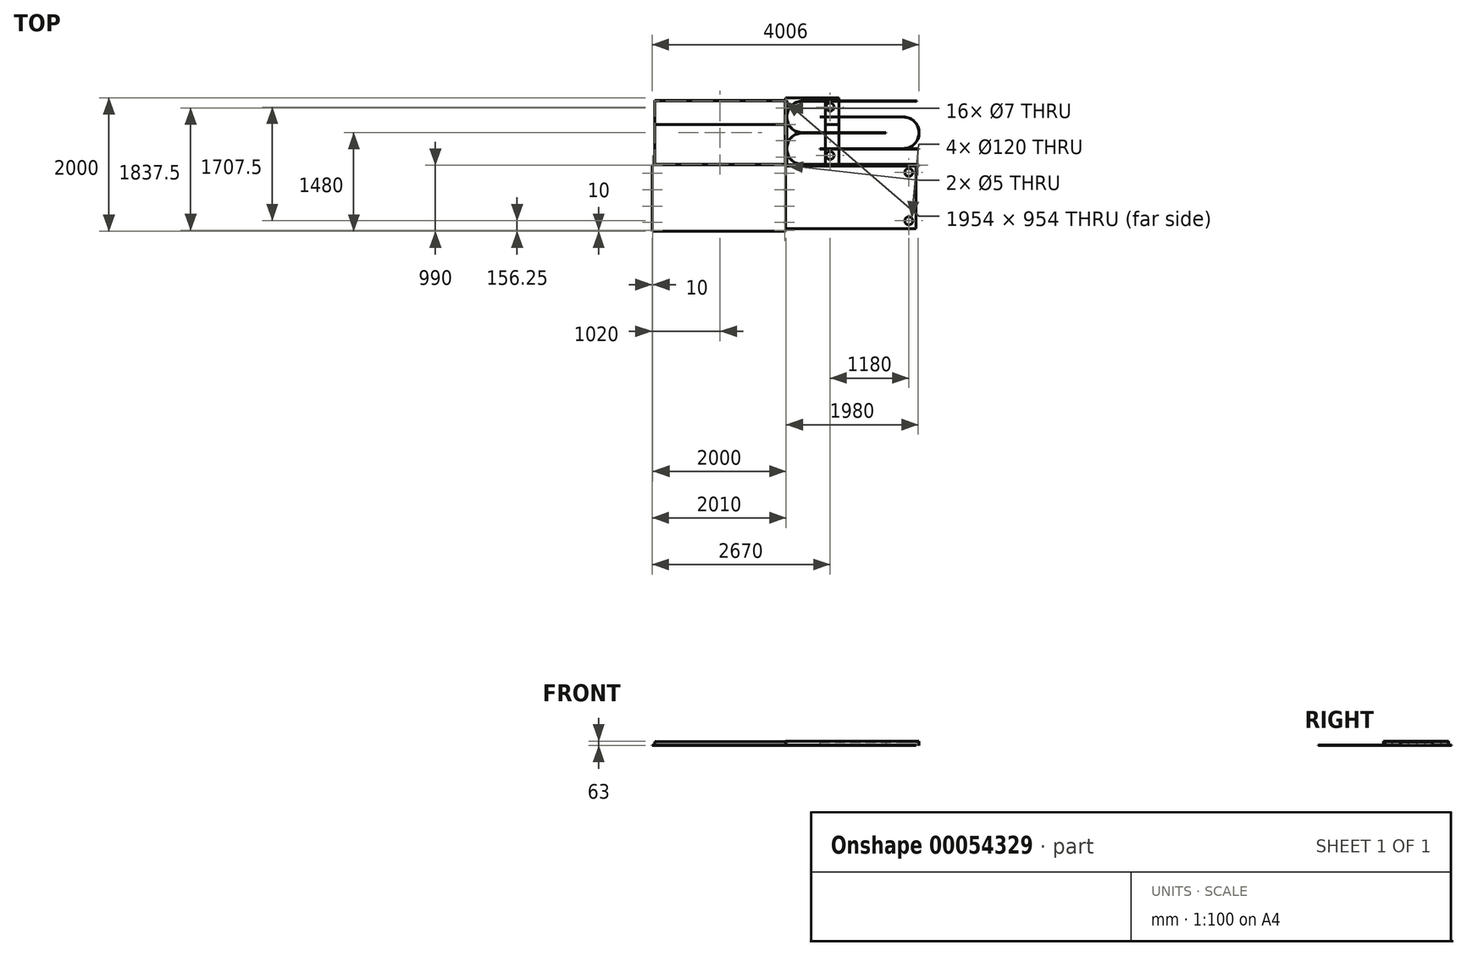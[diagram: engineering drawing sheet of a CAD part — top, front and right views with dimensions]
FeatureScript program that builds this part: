
annotation { "Feature Type Name" : "Feature", "Feature Type Description" : "" }
export const myFeature = defineFeature(function(context is Context, id is Id, definition is map)
    precondition{}
    {
        {
            var Q0;
            Q0=qCreatedBy(makeId("Top.planeOp"),FACE);
            var sketch = newSketch(context, id + "F0", { "sketchPlane" : qUnion([Q0])});
            skLineSegment(sketch, "E0.bottom", {"start": v(0, 0) * mm, "end": v(600, 0) * mm});
            skLineSegment(sketch, "E0.top", {"start": v(0, 1000) * mm, "end": v(600, 1000) * mm});
            skLineSegment(sketch, "E0.left", {"start": v(0, 0) * mm, "end": v(0, 1000) * mm});
            skLineSegment(sketch, "E0.right", {"start": v(600, 0) * mm, "end": v(600, 1000) * mm});
            skSolve(sketch);
        }
        {
            var Q0;
            Q0=makeQuery(id+"F0.imprint","IMPRINT",FACE,{"disambiguationData":[TD([[makeQuery(id+"F0.imprint","IMPRINT",EDGE,{"derivedFrom":sQuery(id+"F0.wireOp",EDGE,"E0.bottom")}),1.0]])]});
            extrude(context, id + "F1", {"entities" : qUnion([Q0]), "depth" : 3 * mm});
        }
        {
            var Q0;
            Q0=qCreatedBy(makeId("Top.planeOp"),FACE);
            var sketch = newSketch(context, id + "F2", { "sketchPlane" : qUnion([Q0])});
            skLineSegment(sketch, "E1.bottom", {"start": v(600, 0) * mm, "end": v(800, 0) * mm});
            skLineSegment(sketch, "E1.top", {"start": v(600, 600) * mm, "end": v(800, 600) * mm});
            skLineSegment(sketch, "E1.left", {"start": v(600, 0) * mm, "end": v(600, 600) * mm});
            skLineSegment(sketch, "E1.right", {"start": v(800, 0) * mm, "end": v(800, 600) * mm});
            skCircle(sketch, "E2", {"center": v(670, 136.25) * mm, "radius": 60 * mm});
            skSolve(sketch);
        }
        {
            var Q0;
            Q0=makeQuery(id+"F2.imprint","IMPRINT",FACE,{"disambiguationData":[TD([[makeQuery(id+"F2.imprint","IMPRINT",EDGE,{"derivedFrom":sQuery(id+"F2.wireOp",EDGE,"E1.bottom")}),1.0]])]});
            extrude(context, id + "F3", {"entities" : qUnion([Q0]), "depth" : 3 * mm});
        }
        {
            var Q0;
            Q0=qCreatedBy(makeId("Top.planeOp"),FACE);
            var sketch = newSketch(context, id + "F4", { "sketchPlane" : qUnion([Q0])});
            skLineSegment(sketch, "E3.bottom", {"start": v(600, 1000) * mm, "end": v(800, 1000) * mm});
            skLineSegment(sketch, "E3.top", {"start": v(600, 600) * mm, "end": v(800, 600) * mm});
            skLineSegment(sketch, "E3.left", {"start": v(600, 1000) * mm, "end": v(600, 600) * mm});
            skLineSegment(sketch, "E3.right", {"start": v(800, 1000) * mm, "end": v(800, 600) * mm});
            skCircle(sketch, "E4", {"center": v(670, 863.75) * mm, "radius": 60 * mm});
            skSolve(sketch);
        }
        {
            var Q0;
            Q0=makeQuery(id+"F4.imprint","IMPRINT",FACE,{"disambiguationData":[TD([[makeQuery(id+"F4.imprint","IMPRINT",EDGE,{"derivedFrom":sQuery(id+"F4.wireOp",EDGE,"E3.bottom")}),-1.0]])]});
            extrude(context, id + "F5", {"entities" : qUnion([Q0]), "depth" : 3 * mm});
        }
        {
            var Q0;
            Q0=makeQuery(id+"F1.opExtrude","CAP_FACE",FACE,{"disambiguationData":[OSD([sQuery(id+"F0.wireOp",EDGE,"E0.bottom"),sQuery(id+"F0.wireOp",EDGE,"E0.top"),sQuery(id+"F0.wireOp",EDGE,"E0.left"),sQuery(id+"F0.wireOp",EDGE,"E0.right")])],"isStart":false});
            var sketch = newSketch(context, id + "F6", { "sketchPlane" : qUnion([Q0])});
            skArc(sketch, "E5", {"start": v(257, 477) * mm, "mid": v(18.5, 238.5) * mm, "end": v(257, 0) * mm});
            skLineSegment(sketch, "E6", {"start": v(257, 0) * mm, "end": v(1972.5, 0) * mm});
            skLineSegment(sketch, "E7", {"start": v(257, 238.5) * mm, "end": v(1240.98, 238.5) * mm, "construction": true});
            skLineSegment(sketch, "E8", {"start": v(257, 477) * mm, "end": v(1510.5, 477) * mm});
            skLineSegment(sketch, "E9.0", {"start": v(257, 474) * mm, "end": v(1510.5, 474) * mm});
            skArc(sketch, "E9.1", {"start": v(257, 474) * mm, "mid": v(21.5, 238.5) * mm, "end": v(257, 3) * mm});
            skLineSegment(sketch, "E9.2", {"start": v(257, 3) * mm, "end": v(1972.5, 3) * mm});
            skLineSegment(sketch, "E10", {"start": v(1510.5, 477) * mm, "end": v(1510.5, 474) * mm});
            skLineSegment(sketch, "E11", {"start": v(1972.5, 3) * mm, "end": v(1972.5, 0) * mm});
            skLineSegment(sketch, "E12.0", {"start": v(257, 475.5) * mm, "end": v(1510.5, 475.5) * mm, "construction": true});
            skArc(sketch, "E12.1", {"start": v(257, 475.5) * mm, "mid": v(20, 238.5) * mm, "end": v(257, 1.5) * mm, "construction": true});
            skLineSegment(sketch, "E12.2", {"start": v(257, 1.5) * mm, "end": v(1972.5, 1.5) * mm, "construction": true});
            skSolve(sketch);
        }
        {
            var Q0;
            {var subQ0=sQuery(id+"F6.wireOp",EDGE,"E10");Q0=makeQuery(id+"F6.imprint","IMPRINT",FACE,{"disambiguationData":[TD([[makeQuery(id+"F6.imprint","IMPRINT",EDGE,{"derivedFrom":subQ0}),-1.0]])]});}
            var Q1;
            {var subQ10=sQuery(id+"F6.wireOp",EDGE,"E9.1");Q1=makeQuery(id+"F6.imprint","IMPRINT",FACE,{"disambiguationData":[TD([[makeQuery(id+"F6.imprint","IMPRINT",EDGE,{"derivedFrom":subQ10}),-1.0]])]});}
            var Q2;
            {var subQ3=sQuery(id+"F6.wireOp",EDGE,"E11");Q2=makeQuery(id+"F6.imprint","IMPRINT",FACE,{"disambiguationData":[TD([[makeQuery(id+"F6.imprint","IMPRINT",EDGE,{"derivedFrom":subQ3}),-1.0]])]});}
            extrude(context, id + "F7", {"entities" : qUnion([Q0, Q1, Q2]), "depth" : 50 * mm});
        }
        {
            var Q0;
            Q0=makeQuery(id+"F7.opExtrude","SWEPT_BODY",BODY,{"disambiguationData":[OSD([sQuery(id+"F6.wireOp",EDGE,"E5"),sQuery(id+"F6.wireOp",EDGE,"E6"),sQuery(id+"F6.wireOp",EDGE,"E8"),sQuery(id+"F6.wireOp",EDGE,"E9.0"),sQuery(id+"F6.wireOp",EDGE,"E9.1"),sQuery(id+"F6.wireOp",EDGE,"E9.2"),sQuery(id+"F6.wireOp",EDGE,"E10"),sQuery(id+"F6.wireOp",EDGE,"E11")])]});
            var Q1;
            Q1=makeQuery(id+"F7.opExtrude","SWEPT_FACE",FACE,{"disambiguationData":[OSD([sQuery(id+"F6.wireOp",EDGE,"E8")])]});
            mirror(context, id + "F8", {"entities" : qUnion([Q0]), "mirrorPlane" : qUnion([Q1])});
        }
        {
            var Q0;
            Q0=qCreatedBy(makeId("Top.planeOp"),FACE);
            var sketch = newSketch(context, id + "F9", { "sketchPlane" : qUnion([Q0])});
            skArc(sketch, "E13", {"start": v(1767.5, 238.5) * mm, "mid": v(2006, 477) * mm, "end": v(1767.5, 715.5) * mm});
            skLineSegment(sketch, "E14", {"start": v(1767.5, 715.5) * mm, "end": v(514, 715.5) * mm});
            skLineSegment(sketch, "E15", {"start": v(1906.7, 477) * mm, "end": v(1767.5, 477) * mm, "construction": true});
            skLineSegment(sketch, "E16.MirrorCS", {"start": v(1767.5, 238.5) * mm, "end": v(514, 238.5) * mm});
            skLineSegment(sketch, "E17.0", {"start": v(1767.5, 712.5) * mm, "end": v(514, 712.5) * mm});
            skArc(sketch, "E17.1", {"start": v(1767.5, 241.5) * mm, "mid": v(2003, 477) * mm, "end": v(1767.5, 712.5) * mm});
            skLineSegment(sketch, "E17.2", {"start": v(1767.5, 241.5) * mm, "end": v(514, 241.5) * mm});
            skLineSegment(sketch, "E18", {"start": v(514, 715.5) * mm, "end": v(514, 712.5) * mm});
            skLineSegment(sketch, "E19", {"start": v(514, 241.5) * mm, "end": v(514, 238.5) * mm});
            skLineSegment(sketch, "E20.0", {"start": v(1767.5, 714) * mm, "end": v(514, 714) * mm, "construction": true});
            skArc(sketch, "E20.1", {"start": v(1767.5, 240) * mm, "mid": v(2004.5, 477) * mm, "end": v(1767.5, 714) * mm, "construction": true});
            skLineSegment(sketch, "E20.2", {"start": v(1767.5, 240) * mm, "end": v(514, 240) * mm, "construction": true});
            skSolve(sketch);
        }
        {
            var Q0;
            Q0=makeQuery(id+"F9.imprint","IMPRINT",FACE,{"disambiguationData":[TD([[makeQuery(id+"F9.imprint","IMPRINT",EDGE,{"derivedFrom":sQuery(id+"F9.wireOp",EDGE,"E13")}),1.0]])]});
            extrude(context, id + "F10", {"entities" : qUnion([Q0]), "depth" : 50 * mm});
        }
        {
            var Q0;
            Q0=qCreatedBy(makeId("Top.planeOp"),FACE);
            var sketch = newSketch(context, id + "F11", { "sketchPlane" : qUnion([Q0])});
            skLineSegment(sketch, "E21.bottom", {"start": v(0, 0) * mm, "end": v(1960, 0) * mm});
            skLineSegment(sketch, "E21.top", {"start": v(0, -960) * mm, "end": v(1960, -960) * mm});
            skLineSegment(sketch, "E21.left", {"start": v(0, -960) * mm, "end": v(0, 0) * mm});
            skLineSegment(sketch, "E21.right", {"start": v(1960, -960) * mm, "end": v(1960, 0) * mm});
            skCircle(sketch, "E22", {"center": v(1850, -843.75) * mm, "radius": 60 * mm});
            skCircle(sketch, "E23", {"center": v(1850, -116.25) * mm, "radius": 60 * mm});
            skSolve(sketch);
        }
        {
            var Q0;
            Q0=makeQuery(id+"F11.imprint","IMPRINT",FACE,{"disambiguationData":[TD([[makeQuery(id+"F11.imprint","IMPRINT",EDGE,{"derivedFrom":sQuery(id+"F11.wireOp",EDGE,"E21.bottom")}),-1.0]])]});
            extrude(context, id + "F12", {"entities" : qUnion([Q0]), "depth" : 3 * mm});
        }
        {
            var Q0;
            Q0=qCreatedBy(makeId("Top.planeOp"),FACE);
            var sketch = newSketch(context, id + "F13", { "sketchPlane" : qUnion([Q0])});
            skLineSegment(sketch, "E24.bottom", {"start": v(0, 0) * mm, "end": v(-1960, 0) * mm});
            skLineSegment(sketch, "E24.top", {"start": v(0, 600) * mm, "end": v(-1960, 600) * mm});
            skLineSegment(sketch, "E24.left", {"start": v(0, 0) * mm, "end": v(0, 600) * mm, "construction": true});
            skLineSegment(sketch, "E24.right", {"start": v(-1960, 0) * mm, "end": v(-1960, 600) * mm});
            skLineSegment(sketch, "E25.bottom", {"start": v(-1960, 600) * mm, "end": v(-1980, 600) * mm, "construction": true});
            skLineSegment(sketch, "E25.top", {"start": v(-1960, 0) * mm, "end": v(-1980, 0) * mm, "construction": true});
            skLineSegment(sketch, "E25.left", {"start": v(-1960, 600) * mm, "end": v(-1960, 0) * mm, "construction": true});
            skLineSegment(sketch, "E25.right", {"start": v(-1980, 600) * mm, "end": v(-1980, 0) * mm, "construction": true});
            skLineSegment(sketch, "E26.bottom", {"start": v(0, 600) * mm, "end": v(20, 600) * mm, "construction": true});
            skLineSegment(sketch, "E26.top", {"start": v(0, 0) * mm, "end": v(20, 0) * mm, "construction": true});
            skLineSegment(sketch, "E26.left", {"start": v(0, 600) * mm, "end": v(0, 0) * mm});
            skLineSegment(sketch, "E26.right", {"start": v(20, 600) * mm, "end": v(20, 0) * mm, "construction": true});
            skSolve(sketch);
        }
        {
            var Q0;
            Q0=makeQuery(id+"F13.imprint","IMPRINT",FACE,{"disambiguationData":[TD([[makeQuery(id+"F13.imprint","IMPRINT",EDGE,{"derivedFrom":sQuery(id+"F13.wireOp",EDGE,"E24.bottom")}),-1.0]])]});
            extrude(context, id + "F14", {"entities" : qUnion([Q0]), "depth" : 1 * mm});
        }
        {
            var Q0;
            Q0=qCreatedBy(makeId("Right.planeOp"),FACE);
            var sketch = newSketch(context, id + "F15", { "sketchPlane" : qUnion([Q0])});
            skLineSegment(sketch, "E27.bottom", {"start": v(-20, 3) * mm, "end": v(0, 3) * mm});
            skLineSegment(sketch, "E27.top", {"start": v(-20, 63) * mm, "end": v(0, 63) * mm});
            skLineSegment(sketch, "E27.left", {"start": v(0, 3) * mm, "end": v(0, 63) * mm});
            skLineSegment(sketch, "E27.right", {"start": v(-20, 3) * mm, "end": v(-20, 63) * mm});
            skSolve(sketch);
        }
        {
            var Q0;
            Q0=makeQuery(id+"F15.imprint","IMPRINT",FACE,{"disambiguationData":[TD([[makeQuery(id+"F15.imprint","IMPRINT",EDGE,{"derivedFrom":sQuery(id+"F15.wireOp",EDGE,"E27.bottom")}),1.0]])]});
            extrude(context, id + "F16", {"entities" : qUnion([Q0]), "depth" : 2000 * mm});
        }
        {
            var Q0;
            Q0=makeQuery(id+"F16.opExtrude","SWEPT_FACE",FACE,{"disambiguationData":[OSD([sQuery(id+"F15.wireOp",EDGE,"E27.top")])]});
            var sketch = newSketch(context, id + "F17", { "sketchPlane" : qUnion([Q0])});
            skPoint(sketch, "E28", {"position": v(10, -10) * mm});
            skPoint(sketch, "E29.1.0.0", {"position": v(1990, -10) * mm});
            skLineSegment(sketch, "E29.direction1", {"start": v(10, -10) * mm, "end": v(1990, -10) * mm, "construction": true});
            skSolve(sketch);
        }
        {
            var Q0;
            Q0=sQuery(id+"F17.wireOp",VERTEX,"E28");
            var Q1;
            Q1=sQuery(id+"F17.wireOp",VERTEX,"E29.1.0.0");
            var Q2;
            Q2=makeQuery(id+"F16.opExtrude","SWEPT_BODY",BODY,{"disambiguationData":[OSD([sQuery(id+"F15.wireOp",EDGE,"E27.bottom"),sQuery(id+"F15.wireOp",EDGE,"E27.top"),sQuery(id+"F15.wireOp",EDGE,"E27.left"),sQuery(id+"F15.wireOp",EDGE,"E27.right")])]});
            hole(context, id + "F18", {"style" : HoleStyle.SIMPLE, "holeDiameter" : 5 * mm, "endStyle" : HoleEndStyle.THROUGH, "locations" : qUnion([Q0, Q1]), "scope" : qUnion([Q2])});
        }
        {
            var Q0;
            Q0=qCreatedBy(makeId("Front.planeOp"),FACE);
            var sketch = newSketch(context, id + "F19", { "sketchPlane" : qUnion([Q0])});
            skLineSegment(sketch, "E30.bottom", {"start": v(20, 63) * mm, "end": v(0, 63) * mm});
            skLineSegment(sketch, "E30.top", {"start": v(20, 3) * mm, "end": v(0, 3) * mm});
            skLineSegment(sketch, "E30.left", {"start": v(20, 63) * mm, "end": v(20, 3) * mm});
            skLineSegment(sketch, "E30.right", {"start": v(0, 63) * mm, "end": v(0, 3) * mm});
            skSolve(sketch);
        }
        {
            var Q0;
            Q0=makeQuery(id+"F19.imprint","IMPRINT",FACE,{"disambiguationData":[TD([[makeQuery(id+"F19.imprint","IMPRINT",EDGE,{"derivedFrom":sQuery(id+"F19.wireOp",EDGE,"E30.bottom")}),1.0]])]});
            extrude(context, id + "F20", {"entities" : qUnion([Q0]), "oppositeDirection" : true, "depth" : (1000 - 40) * mm});
        }
        {
            var Q0;
            Q0=makeQuery(id+"F20.opExtrude","SWEPT_FACE",FACE,{"disambiguationData":[OSD([sQuery(id+"F19.wireOp",EDGE,"E30.bottom")])]});
            var sketch = newSketch(context, id + "F21", { "sketchPlane" : qUnion([Q0])});
            skPoint(sketch, "E31", {"position": v(10, 112.5) * mm});
            skPoint(sketch, "E32.0.1.0", {"position": v(10, 357.5) * mm});
            skPoint(sketch, "E32.0.2.0", {"position": v(10, 602.5) * mm});
            skPoint(sketch, "E32.0.3.0", {"position": v(10, 847.5) * mm});
            skLineSegment(sketch, "E32.direction1", {"start": v(10, 112.5) * mm, "end": v(35, 112.5) * mm, "construction": true});
            skLineSegment(sketch, "E32.direction2", {"start": v(10, 112.5) * mm, "end": v(10, 357.5) * mm, "construction": true});
            skSolve(sketch);
        }
        {
            var Q0;
            Q0=sQuery(id+"F21.wireOp",VERTEX,"E31");
            var Q1;
            Q1=sQuery(id+"F21.wireOp",VERTEX,"E32.0.1.0");
            var Q2;
            Q2=sQuery(id+"F21.wireOp",VERTEX,"E32.0.2.0");
            var Q3;
            Q3=sQuery(id+"F21.wireOp",VERTEX,"E32.0.3.0");
            var Q4;
            Q4=makeQuery(id+"F20.opExtrude","SWEPT_BODY",BODY,{"disambiguationData":[OSD([sQuery(id+"F19.wireOp",EDGE,"E30.bottom"),sQuery(id+"F19.wireOp",EDGE,"E30.top"),sQuery(id+"F19.wireOp",EDGE,"E30.left"),sQuery(id+"F19.wireOp",EDGE,"E30.right")])]});
            hole(context, id + "F22", {"style" : HoleStyle.SIMPLE, "holeDiameter" : 7 * mm, "endStyle" : HoleEndStyle.THROUGH, "locations" : qUnion([Q0, Q1, Q2, Q3]), "scope" : qUnion([Q4])});
        }
        {
            var Q0;
            Q0=qCreatedBy(makeId("Top.planeOp"),FACE);
            var sketch = newSketch(context, id + "F23", { "sketchPlane" : qUnion([Q0])});
            skLineSegment(sketch, "E33.bottom", {"start": v(0, 0) * mm, "end": v(-2000, 0) * mm});
            skLineSegment(sketch, "E33.top", {"start": v(0, -1000) * mm, "end": v(-2000, -1000) * mm});
            skLineSegment(sketch, "E33.left", {"start": v(0, 0) * mm, "end": v(0, -1000) * mm});
            skLineSegment(sketch, "E33.right", {"start": v(-2000, 0) * mm, "end": v(-2000, -1000) * mm});
            skSolve(sketch);
        }
        {
            var Q0;
            Q0=makeQuery(id+"F23.imprint","IMPRINT",FACE,{"disambiguationData":[TD([[makeQuery(id+"F23.imprint","IMPRINT",EDGE,{"derivedFrom":sQuery(id+"F23.wireOp",EDGE,"E33.bottom")}),1.0]])]});
            extrude(context, id + "F24", {"entities" : qUnion([Q0]), "depth" : 3 * mm});
        }
        {
            var Q0;
            Q0=makeQuery(id+"F24.opExtrude","CAP_FACE",FACE,{"disambiguationData":[OSD([sQuery(id+"F23.wireOp",EDGE,"E33.bottom"),sQuery(id+"F23.wireOp",EDGE,"E33.top"),sQuery(id+"F23.wireOp",EDGE,"E33.left"),sQuery(id+"F23.wireOp",EDGE,"E33.right")])],"isStart":false});
            var sketch = newSketch(context, id + "F25", { "sketchPlane" : qUnion([Q0])});
            skPoint(sketch, "E34", {"position": v(-1990, -990) * mm});
            skPoint(sketch, "E35.0.1.0", {"position": v(-1990, -10) * mm});
            skPoint(sketch, "E35.1.0.0", {"position": v(-10, -990) * mm});
            skPoint(sketch, "E35.1.1.0", {"position": v(-10, -10) * mm});
            skLineSegment(sketch, "E35.direction1", {"start": v(-1990, -990) * mm, "end": v(-10, -990) * mm, "construction": true});
            skLineSegment(sketch, "E35.direction2", {"start": v(-1990, -990) * mm, "end": v(-1990, -10) * mm, "construction": true});
            skPoint(sketch, "E36", {"position": v(-1990, -867.5) * mm});
            skPoint(sketch, "E37.0.1.0", {"position": v(-1990, -622.5) * mm});
            skPoint(sketch, "E37.0.2.0", {"position": v(-1990, -377.5) * mm});
            skPoint(sketch, "E37.0.3.0", {"position": v(-1990, -132.5) * mm});
            skLineSegment(sketch, "E37.direction1", {"start": v(-1990, -867.5) * mm, "end": v(-10, -867.5) * mm, "construction": true});
            skLineSegment(sketch, "E37.direction2", {"start": v(-1990, -867.5) * mm, "end": v(-1990, -622.5) * mm, "construction": true});
            skPoint(sketch, "E38.0.1.0", {"position": v(-10, -867.5) * mm});
            skPoint(sketch, "E38.0.1.1", {"position": v(-10, -622.5) * mm});
            skPoint(sketch, "E38.0.1.2", {"position": v(-10, -377.5) * mm});
            skPoint(sketch, "E38.0.1.3", {"position": v(-10, -132.5) * mm});
            skSolve(sketch);
        }
        {
            var Q0;
            Q0=sQuery(id+"F25.wireOp",VERTEX,"E34");
            var Q1;
            Q1=sQuery(id+"F25.wireOp",VERTEX,"E36");
            var Q2;
            Q2=sQuery(id+"F25.wireOp",VERTEX,"E37.0.1.0");
            var Q3;
            Q3=sQuery(id+"F25.wireOp",VERTEX,"E37.0.2.0");
            var Q4;
            Q4=sQuery(id+"F25.wireOp",VERTEX,"E37.0.3.0");
            var Q5;
            Q5=sQuery(id+"F25.wireOp",VERTEX,"E35.0.1.0");
            var Q6;
            Q6=sQuery(id+"F25.wireOp",VERTEX,"E35.1.1.0");
            var Q7;
            Q7=sQuery(id+"F25.wireOp",VERTEX,"E35.1.0.0");
            var Q8;
            Q8=sQuery(id+"F25.wireOp",VERTEX,"E38.0.1.0");
            var Q9;
            Q9=sQuery(id+"F25.wireOp",VERTEX,"E38.0.1.1");
            var Q10;
            Q10=sQuery(id+"F25.wireOp",VERTEX,"E38.0.1.2");
            var Q11;
            Q11=sQuery(id+"F25.wireOp",VERTEX,"E38.0.1.3");
            var Q12;
            Q12=makeQuery(id+"F24.opExtrude","SWEPT_BODY",BODY,{"disambiguationData":[OSD([sQuery(id+"F23.wireOp",EDGE,"E33.bottom"),sQuery(id+"F23.wireOp",EDGE,"E33.top"),sQuery(id+"F23.wireOp",EDGE,"E33.left"),sQuery(id+"F23.wireOp",EDGE,"E33.right")])]});
            hole(context, id + "F26", {"style" : HoleStyle.SIMPLE, "holeDiameter" : 7 * mm, "endStyle" : HoleEndStyle.THROUGH, "locations" : qUnion([Q0, Q1, Q2, Q3, Q4, Q5, Q6, Q7, Q8, Q9, Q10, Q11]), "scope" : qUnion([Q12])});
        }
        {
            var Q0;
            Q0=qCreatedBy(makeId("Top.planeOp"),FACE);
            var sketch = newSketch(context, id + "F27", { "sketchPlane" : qUnion([Q0])});
            skLineSegment(sketch, "E39.bottom", {"start": v(0, 960) * mm, "end": v(-1960, 960) * mm});
            skLineSegment(sketch, "E39.top", {"start": v(0, 0) * mm, "end": v(-1960, 0) * mm});
            skLineSegment(sketch, "E39.left", {"start": v(0, 960) * mm, "end": v(0, 0) * mm});
            skLineSegment(sketch, "E39.right", {"start": v(-1960, 960) * mm, "end": v(-1960, 0) * mm});
            skLineSegment(sketch, "E40.0", {"start": v(-3, 957) * mm, "end": v(-1957, 957) * mm});
            skLineSegment(sketch, "E40.1", {"start": v(-3, 957) * mm, "end": v(-3, 3) * mm});
            skLineSegment(sketch, "E40.2", {"start": v(-3, 3) * mm, "end": v(-1957, 3) * mm});
            skLineSegment(sketch, "E40.3", {"start": v(-1957, 957) * mm, "end": v(-1957, 3) * mm});
            skSolve(sketch);
        }
        {
            var Q0;
            Q0=makeQuery(id+"F27.imprint","IMPRINT",FACE,{"disambiguationData":[TD([[makeQuery(id+"F27.imprint","IMPRINT",EDGE,{"derivedFrom":sQuery(id+"F27.wireOp",EDGE,"E39.bottom")}),1.0]])]});
            extrude(context, id + "F28", {"entities" : qUnion([Q0]), "depth" : 57 * mm});
        }
        {
            var Q0;
            Q0=qCreatedBy(makeId("Top.planeOp"),FACE);
            var sketch = newSketch(context, id + "F29", { "sketchPlane" : qUnion([Q0])});
            skLineSegment(sketch, "E41.bottom", {"start": v(514, 238.5) * mm, "end": v(2006, 238.5) * mm});
            skLineSegment(sketch, "E41.top", {"start": v(514, 235.5) * mm, "end": v(2006, 235.5) * mm});
            skLineSegment(sketch, "E41.left", {"start": v(514, 238.5) * mm, "end": v(514, 235.5) * mm});
            skLineSegment(sketch, "E41.right", {"start": v(2006, 238.5) * mm, "end": v(2006, 235.5) * mm});
            skSolve(sketch);
        }
        {
            var Q0;
            Q0=makeQuery(id+"F29.imprint","IMPRINT",FACE,{"disambiguationData":[TD([[makeQuery(id+"F29.imprint","IMPRINT",EDGE,{"derivedFrom":sQuery(id+"F29.wireOp",EDGE,"E41.bottom")}),-1.0]])]});
            extrude(context, id + "F30", {"entities" : qUnion([Q0]), "depth" : 50 * mm});
        }
    });
